# Revit family: Gira_207500
name_source: partatom
category: Elektroinstallationen
revit_build: Autodesk Revit 2017 (Build: 20160225_1515(x64)
units: mm (PartAtom-declared; Revit-internal decimal feet)

## family parameters
Basisbauteil = Fläche
Beim Laden mit Abzugskörper schneiden = Nein
Bemaßung runder Anschluss = Durchmesser verwenden
Beschriftungsausrichtung beibehalten = Nein
Gemeinsam genutzt = Nein
Raumberechnungspunkt = Nein
Teiletyp = Normal

## types (1)
- Gira_207500
    BIM = https://media.stage.bim.site
    Beschreibung = Gira FacilityServer Serv.,Gira FacilityServer,,,Gateway for the KNX installation, specifically matched to the demanding requirements in the commercial sector. With the Gira FacilityServer, systems and building functions can be networked intelligently with each other and the entire KNX installation can be monitored, controlled and programmed centrally from a PC. Access and monitoring of the building and system technology from outside is also possible by connecting to the Internet. Also serves as a data server for higher-level facility management systems, to which it provides stored consumption and operating data for evaluation. It offers the complete functional range of the Gira HomeServer, but is equipped with considerably more memory capacity for its use in the commercial sector. This enables considerably larger amounts of data to be stored and more complex, more extensive visualisations to be created. Several Gira FacilityServers can be networked in order to interconnect buildings which are spatially separated from each other: Local and higher-level applications can be combined. In addition to a PC, access is also possible via other Internet-capable devices connected to LAN, WLAN, or the internet. As a result, KNX functions can be controlled and regulated anywhere. The Gira Control 9 Client, Gira Control 19 Client 2 and the Gira HomeServer app can be used as convenient operating devices. The app is available from the Apple App Store and Google Play Store and can be used on smartphones and tablets.,,Features:,- Can be updated.,- Installation in 19 rack. For this purpose the scope of supply includes a 19 insert unit with an aluminium plate. Can also be used as a stand-alone device.,- Management of 200 users. Multiple logins possible under one user name.,- Project archiving with individual content such as floor plans, etc.,- Cyclic triggered data recording (for example, temperature courses, elapsed-hours meters, fill levels).,- Graphic user interface: Visualisation of building and device states with freely positionable icons and texts. Saving of individual images and menu structures for each user group.,- Evaluation of IP cameras: Recording of images and playback in the visualisation. Forwarding of footage and images via email and FTP. National requirements, e.g. protocol-specific information and communications standards need to be observed.,- Exporting of data or alarm records in the Excel(tm), CSV, HTML or XML file formats.,- Mathematical functions (e.g. basic operations).,- Storing and calling up of light scenes.,- Timers, weekly program, public holiday calendar.,- Fault messages, measured values and sensor or actuator states can be transmitted by push notification and e-mail. Acknowledgement via KNX.,- Self-teaching occupied-home simulation.,- Remote programming via network, Internet and data communications connections.,- Transmitting ASCII texts.,- IP coupling with products from other manufacturers that generate or edit IP telegrams for control.,- Low-wearing.,- Graphic logic editor: Allows for example copying module groups across projects, creating any number of work sheets. Over 150 logic nodes are set up.,- Importing and exporting of global libraries.,- Communication objects: Data transfer from ETS by means of OPC or directly from the knxproj file. Import and export of communication objects as CSV file.,- Universal timer: Several switching points possible per clock. Use of placeholders in day, month, year. Activation deactivation via communication object. With Astro and random function.,- Data backup restoration of retentive data.,- 14-byte KNX texts: Evaluation by comparison with text string. Use in push notification, e-mails, or status page.,- Receipt of IP telegrams: Specification of an address range, extraction of 14-byte KNX texts, assignment to 14-byte KNX texts.,- SNMP: Reading out numeric and 14-byte KNX texts. Setting numeric values, integer values, and texts. Transmitting SNMP Traps via FacilityServer command. Optional ColdStart Trap when starting the FacilityServer.,- Operation status display via Agfeo telephone system.,- Evaluation of web-based IP devices (reading writing).,- Bus access via KNXnet IP protocol.,- iETS server: Remote programming of KNX systems. Enabling of iETS function with a communication object. Gira HomeServer continues to run without restriction during programming via iETS. Switching processes continue to run. Process image remains current.,,Notes :,- Further information: www.gira.de facilityserver.,- Technical information may vary or be modified depending on version. In the same way, the scope of service can vary among the individual clients (QuadClient, iOS app, Android app).,- Recommended system requirements for operating devices: Internet browser of possible operating devices must support at least HTML 4.0, Java Script 1.1, CSS, and Dynamic HTML.,- Gira FacilityServer Expert software for operating systems from Windows XP(tm) including Internet Explorer from Version 6.0.,- Adoption of the ETS group addresses from ETS 2, 3, 4, and 5.,- Integration of graphics programs.
    Data sheet = https://katalog.gira.de
    GTIN = 4010337051817
    HAN = 207500
    Hersteller = Gira
    Productwebsite = http://katalog.gira.de
    Type of accessory = Other
    Typname = Gira FacilityServer Gira Server
    URL = https://www.gira.de
    Vorgabe-Ansicht = 1219 mm

## geometry (parser evidence)
native form markers: Sweep x2
no freeform markers — native parametric forms only
